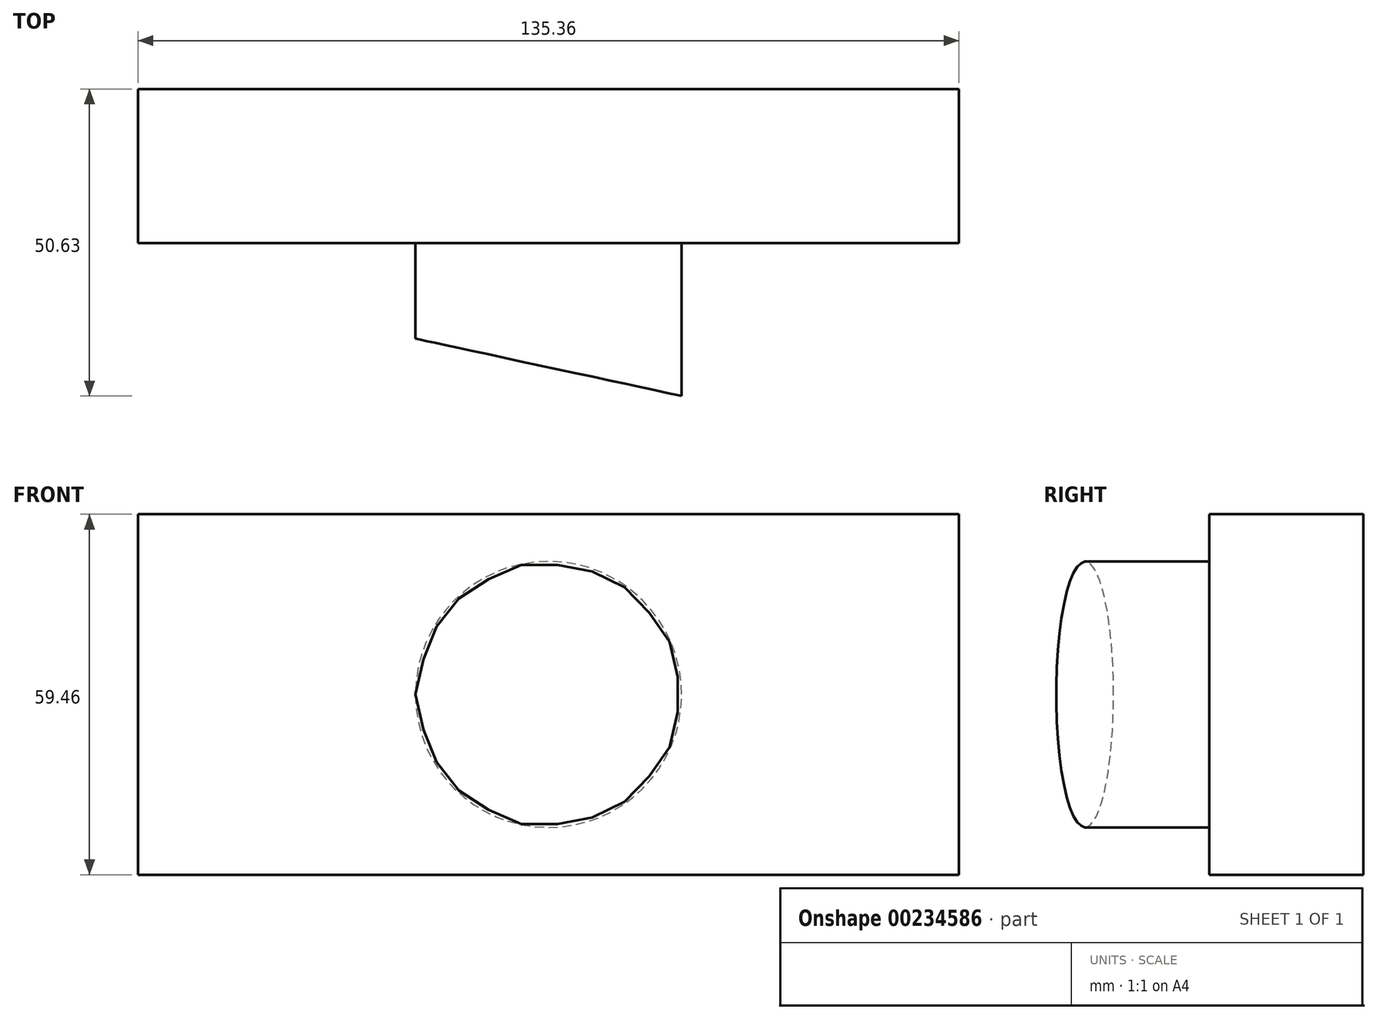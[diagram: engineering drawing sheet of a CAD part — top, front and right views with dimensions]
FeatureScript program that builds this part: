
annotation { "Feature Type Name" : "Feature", "Feature Type Description" : "" }
export const myFeature = defineFeature(function(context is Context, id is Id, definition is map)
    precondition{}
    {
        {
            var Q0;
            Q0=qCreatedBy(makeId("Front.planeOp"),FACE);
            var sketch = newSketch(context, id + "F0", { "sketchPlane" : qUnion([Q0])});
            skLineSegment(sketch, "E0.bottom", {"start": v(67.68, 29.73) * mm, "end": v(-67.68, 29.73) * mm});
            skLineSegment(sketch, "E0.top", {"start": v(67.68, -29.73) * mm, "end": v(-67.68, -29.73) * mm});
            skLineSegment(sketch, "E0.left", {"start": v(67.68, 29.73) * mm, "end": v(67.68, -29.73) * mm});
            skLineSegment(sketch, "E0.right", {"start": v(-67.68, 29.73) * mm, "end": v(-67.68, -29.73) * mm});
            skPoint(sketch, "E0.middle", {"position": v(0, 0) * mm});
            skSolve(sketch);
        }
        {
            var Q0;
            Q0=makeQuery(id+"F0.imprint","IMPRINT",FACE,{"disambiguationData":[TD([[makeQuery(id+"F0.imprint","IMPRINT",EDGE,{"derivedFrom":sQuery(id+"F0.wireOp",EDGE,"E0.bottom")}),1.0]])]});
            extrude(context, id + "F1", {"entities" : qUnion([Q0]), "depth" : 25.4 * mm});
        }
        {
            var Q0;
            Q0=makeQuery(id+"F1.opExtrude","CAP_FACE",FACE,{"disambiguationData":[OSD([sQuery(id+"F0.wireOp",EDGE,"E0.bottom"),sQuery(id+"F0.wireOp",EDGE,"E0.top"),sQuery(id+"F0.wireOp",EDGE,"E0.left"),sQuery(id+"F0.wireOp",EDGE,"E0.right")])],"isStart":false});
            var sketch = newSketch(context, id + "F2", { "sketchPlane" : qUnion([Q0])});
            skCircle(sketch, "E1", {"center": v(0, 0) * mm, "radius": 21.94 * mm});
            skSolve(sketch);
        }
        {
            var Q0;
            Q0 = qSketchRegion(id + "F2", true);
            extrude(context, id + "F3", {"entities" : qUnion([Q0]), "operationType" : NewBodyOperationType.ADD, "depth" : 25.4 * mm});
        }
        {
            var Q0;
            Q0=qCreatedBy(makeId("Top.planeOp"),FACE);
            var sketch = newSketch(context, id + "F4", { "sketchPlane" : qUnion([Q0])});
            skLineSegment(sketch, "E2", {"start": v(-24.17, -40.69) * mm, "end": v(34.16, -53.26) * mm});
            skLineSegment(sketch, "E3", {"start": v(-24.17, -53.26) * mm, "end": v(34.16, -53.26) * mm});
            skLineSegment(sketch, "E4", {"start": v(-24.17, -40.69) * mm, "end": v(-24.17, -53.26) * mm});
            skSolve(sketch);
        }
        {
            var Q0;
            Q0 = qSketchRegion(id + "F4", true);
            extrude(context, id + "F5", {"entities" : qUnion([Q0]), "operationType" : NewBodyOperationType.REMOVE, "depth" : 25.4 * mm, "hasSecondDirection" : true, "secondDirectionOppositeDirection" : true, "secondDirectionDepth" : 25.4 * mm});
        }
    });
